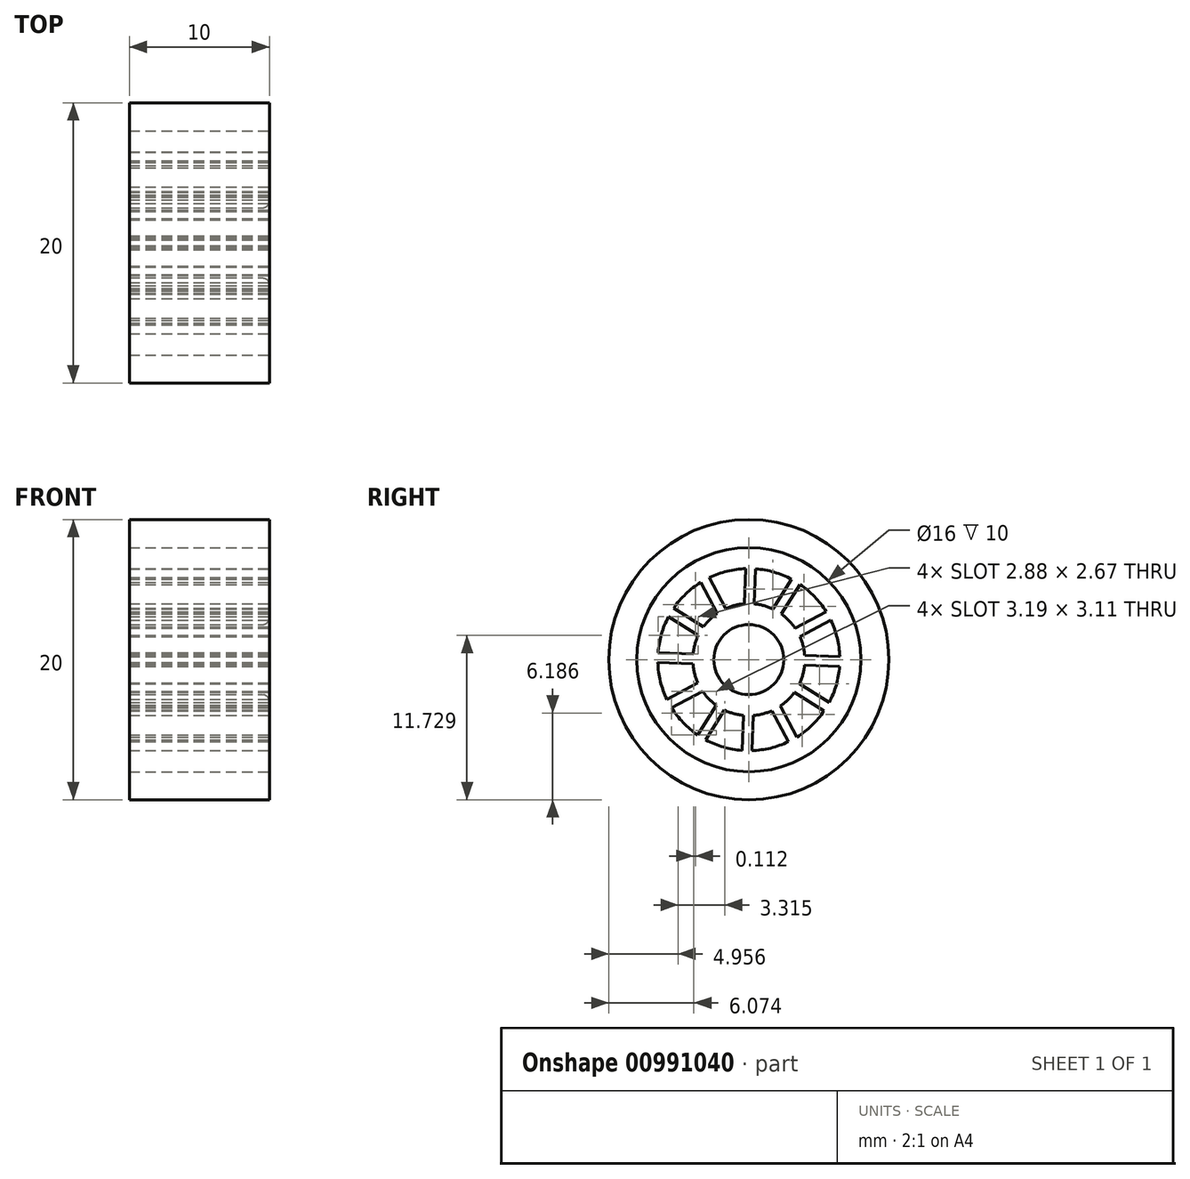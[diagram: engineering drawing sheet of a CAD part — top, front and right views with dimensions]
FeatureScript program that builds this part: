
annotation { "Feature Type Name" : "Feature", "Feature Type Description" : "" }
export const myFeature = defineFeature(function(context is Context, id is Id, definition is map)
    precondition{}
    {
        {
            var Q0;
            Q0=qCreatedBy(makeId("Right.planeOp"),FACE);
            var sketch = newSketch(context, id + "F0", { "sketchPlane" : qUnion([Q0])});
            skCircle(sketch, "E0", {"center": v(0, 0) * mm, "radius": 10 * mm});
            skCircle(sketch, "E1", {"center": v(0, 0) * mm, "radius": 8 * mm});
            skArc(sketch, "E2", {"start": v(-0.21, 6.5) * mm, "mid": v(-1.55, 6.31) * mm, "end": v(-2.82, 5.86) * mm});
            skArc(sketch, "E3", {"start": v(-0.3, 3.99) * mm, "mid": v(-1, 3.88) * mm, "end": v(-1.65, 3.64) * mm});
            skCircle(sketch, "E4", {"center": v(0, 0) * mm, "radius": 2.5 * mm});
            skLineSegment(sketch, "E5.left", {"start": v(0.49, 6.48) * mm, "end": v(0.4, 3.98) * mm});
            skLineSegment(sketch, "E5.right", {"start": v(-0.21, 6.5) * mm, "end": v(-0.3, 3.99) * mm});
            skPoint(sketch, "E5.middle", {"position": v(0, 2.76) * mm});
            skPoint(sketch, "E6.orphan", {"position": v(-0.32, 3.46) * mm});
            skPoint(sketch, "E7.orphan", {"position": v(0.37, 3.43) * mm});
            skPoint(sketch, "E8.orphan", {"position": v(-0.37, 2.08) * mm});
            skPoint(sketch, "E9.orphan", {"position": v(0.32, 2.06) * mm});
            skLineSegment(sketch, "E10.1.0", {"start": v(-3.43, 5.52) * mm, "end": v(-2.26, 3.3) * mm});
            skLineSegment(sketch, "E10.1.1", {"start": v(-2.82, 5.86) * mm, "end": v(-1.65, 3.64) * mm});
            skLineSegment(sketch, "E10.2.0", {"start": v(-5.73, 3.06) * mm, "end": v(-3.6, 1.73) * mm});
            skLineSegment(sketch, "E10.2.1", {"start": v(-5.37, 3.66) * mm, "end": v(-3.25, 2.33) * mm});
            skLineSegment(sketch, "E10.3.0", {"start": v(-6.5, -0.21) * mm, "end": v(-3.99, -0.3) * mm});
            skLineSegment(sketch, "E10.3.1", {"start": v(-6.48, 0.49) * mm, "end": v(-3.98, 0.4) * mm});
            skLineSegment(sketch, "E10.4.0", {"start": v(-5.52, -3.43) * mm, "end": v(-3.3, -2.26) * mm});
            skLineSegment(sketch, "E10.4.1", {"start": v(-5.86, -2.82) * mm, "end": v(-3.64, -1.65) * mm});
            skLineSegment(sketch, "E10.5.0", {"start": v(-3.06, -5.73) * mm, "end": v(-1.73, -3.6) * mm});
            skLineSegment(sketch, "E10.5.1", {"start": v(-3.66, -5.37) * mm, "end": v(-2.33, -3.25) * mm});
            skLineSegment(sketch, "E10.6.0", {"start": v(0.21, -6.5) * mm, "end": v(0.3, -3.99) * mm});
            skLineSegment(sketch, "E10.6.1", {"start": v(-0.49, -6.48) * mm, "end": v(-0.4, -3.98) * mm});
            skLineSegment(sketch, "E10.7.0", {"start": v(3.43, -5.52) * mm, "end": v(2.26, -3.3) * mm});
            skLineSegment(sketch, "E10.7.1", {"start": v(2.82, -5.86) * mm, "end": v(1.65, -3.64) * mm});
            skLineSegment(sketch, "E10.8.0", {"start": v(5.73, -3.06) * mm, "end": v(3.6, -1.73) * mm});
            skLineSegment(sketch, "E10.8.1", {"start": v(5.37, -3.66) * mm, "end": v(3.25, -2.33) * mm});
            skLineSegment(sketch, "E10.9.0", {"start": v(6.5, 0.21) * mm, "end": v(3.99, 0.3) * mm});
            skLineSegment(sketch, "E10.9.1", {"start": v(6.48, -0.49) * mm, "end": v(3.98, -0.4) * mm});
            skLineSegment(sketch, "E10.10.0", {"start": v(5.52, 3.43) * mm, "end": v(3.3, 2.26) * mm});
            skLineSegment(sketch, "E10.10.1", {"start": v(5.86, 2.82) * mm, "end": v(3.64, 1.65) * mm});
            skLineSegment(sketch, "E10.11.0", {"start": v(3.06, 5.73) * mm, "end": v(1.73, 3.6) * mm});
            skLineSegment(sketch, "E10.11.1", {"start": v(3.66, 5.37) * mm, "end": v(2.33, 3.25) * mm});
            skArc(sketch, "E11.trimOffspring", {"start": v(3.06, 5.73) * mm, "mid": v(1.81, 6.24) * mm, "end": v(0.49, 6.48) * mm});
            skArc(sketch, "E12.trimOffspring", {"start": v(1.73, 3.6) * mm, "mid": v(1.08, 3.85) * mm, "end": v(0.4, 3.98) * mm});
            skArc(sketch, "E13.trimOffspring", {"start": v(5.52, 3.43) * mm, "mid": v(4.7, 4.5) * mm, "end": v(3.66, 5.37) * mm});
            skArc(sketch, "E14.trimOffspring", {"start": v(3.3, 2.26) * mm, "mid": v(2.86, 2.8) * mm, "end": v(2.33, 3.25) * mm});
            skArc(sketch, "E15.trimOffspring", {"start": v(6.5, 0.21) * mm, "mid": v(6.31, 1.55) * mm, "end": v(5.86, 2.82) * mm});
            skArc(sketch, "E16.trimOffspring", {"start": v(3.99, 0.3) * mm, "mid": v(3.88, 1) * mm, "end": v(3.64, 1.65) * mm});
            skArc(sketch, "E17.trimOffspring", {"start": v(3.6, -1.73) * mm, "mid": v(3.85, -1.08) * mm, "end": v(3.98, -0.4) * mm});
            skArc(sketch, "E18.trimOffspring", {"start": v(5.73, -3.06) * mm, "mid": v(6.24, -1.81) * mm, "end": v(6.48, -0.49) * mm});
            skArc(sketch, "E19.trimOffspring", {"start": v(-3.43, 5.52) * mm, "mid": v(-4.5, 4.7) * mm, "end": v(-5.37, 3.66) * mm});
            skArc(sketch, "E20.trimOffspring", {"start": v(-2.26, 3.3) * mm, "mid": v(-2.8, 2.86) * mm, "end": v(-3.25, 2.33) * mm});
            skArc(sketch, "E21.trimOffspring", {"start": v(-3.6, 1.73) * mm, "mid": v(-3.85, 1.08) * mm, "end": v(-3.98, 0.4) * mm});
            skArc(sketch, "E22.trimOffspring", {"start": v(-5.73, 3.06) * mm, "mid": v(-6.24, 1.81) * mm, "end": v(-6.48, 0.49) * mm});
            skArc(sketch, "E23.trimOffspring", {"start": v(-6.5, -0.21) * mm, "mid": v(-6.31, -1.55) * mm, "end": v(-5.86, -2.82) * mm});
            skArc(sketch, "E24.trimOffspring", {"start": v(-3.99, -0.3) * mm, "mid": v(-3.88, -1) * mm, "end": v(-3.64, -1.65) * mm});
            skArc(sketch, "E25.trimOffspring", {"start": v(-5.52, -3.43) * mm, "mid": v(-4.7, -4.5) * mm, "end": v(-3.66, -5.37) * mm});
            skArc(sketch, "E26.trimOffspring", {"start": v(-3.3, -2.26) * mm, "mid": v(-2.86, -2.8) * mm, "end": v(-2.33, -3.25) * mm});
            skArc(sketch, "E27.trimOffspring", {"start": v(-1.73, -3.6) * mm, "mid": v(-1.08, -3.85) * mm, "end": v(-0.4, -3.98) * mm});
            skArc(sketch, "E28.trimOffspring", {"start": v(-3.06, -5.73) * mm, "mid": v(-1.81, -6.24) * mm, "end": v(-0.49, -6.48) * mm});
            skArc(sketch, "E29.trimOffspring", {"start": v(0.3, -3.99) * mm, "mid": v(1, -3.88) * mm, "end": v(1.65, -3.64) * mm});
            skArc(sketch, "E30.trimOffspring", {"start": v(0.21, -6.5) * mm, "mid": v(1.55, -6.31) * mm, "end": v(2.82, -5.86) * mm});
            skArc(sketch, "E31.trimOffspring", {"start": v(2.26, -3.3) * mm, "mid": v(2.8, -2.86) * mm, "end": v(3.25, -2.33) * mm});
            skArc(sketch, "E32.trimOffspring", {"start": v(3.43, -5.52) * mm, "mid": v(4.5, -4.7) * mm, "end": v(5.37, -3.66) * mm});
            skSolve(sketch);
        }
        {
            var Q0;
            Q0=makeQuery(id+"F0.imprint","IMPRINT",FACE,{"disambiguationData":[TD([[makeQuery(id+"F0.imprint","IMPRINT",EDGE,{"derivedFrom":sQuery(id+"F0.wireOp",EDGE,"E0")}),1.0]])]});
            extrude(context, id + "F1", {"entities" : qUnion([Q0]), "oppositeDirection" : true, "depth" : 10 * mm, "offsetDistance" : 25 * mm});
        }
        {
            var Q0;
            Q0=makeQuery(id+"F0.imprint","IMPRINT",FACE,{"disambiguationData":[TD([[makeQuery(id+"F0.imprint","IMPRINT",EDGE,{"derivedFrom":sQuery(id+"F0.wireOp",EDGE,"E1")}),1.0]])]});
            extrude(context, id + "F2", {"entities" : qUnion([Q0]), "oppositeDirection" : true, "depth" : 10 * mm, "offsetDistance" : 25 * mm});
        }
        {
            var Q0;
            Q0=makeQuery(id+"F2.opExtrude","CAP_EDGE",EDGE,{"disambiguationData":[OSD([sQuery(id+"F0.wireOp",EDGE,"E4")])],"isStart":true});
            fillet(context, id + "F3", {"entities" : qUnion([Q0]), "radius" : .5 * mm, "tangentPropagation" : true, "allowEdgeOverflow" : false});
        }
    });
